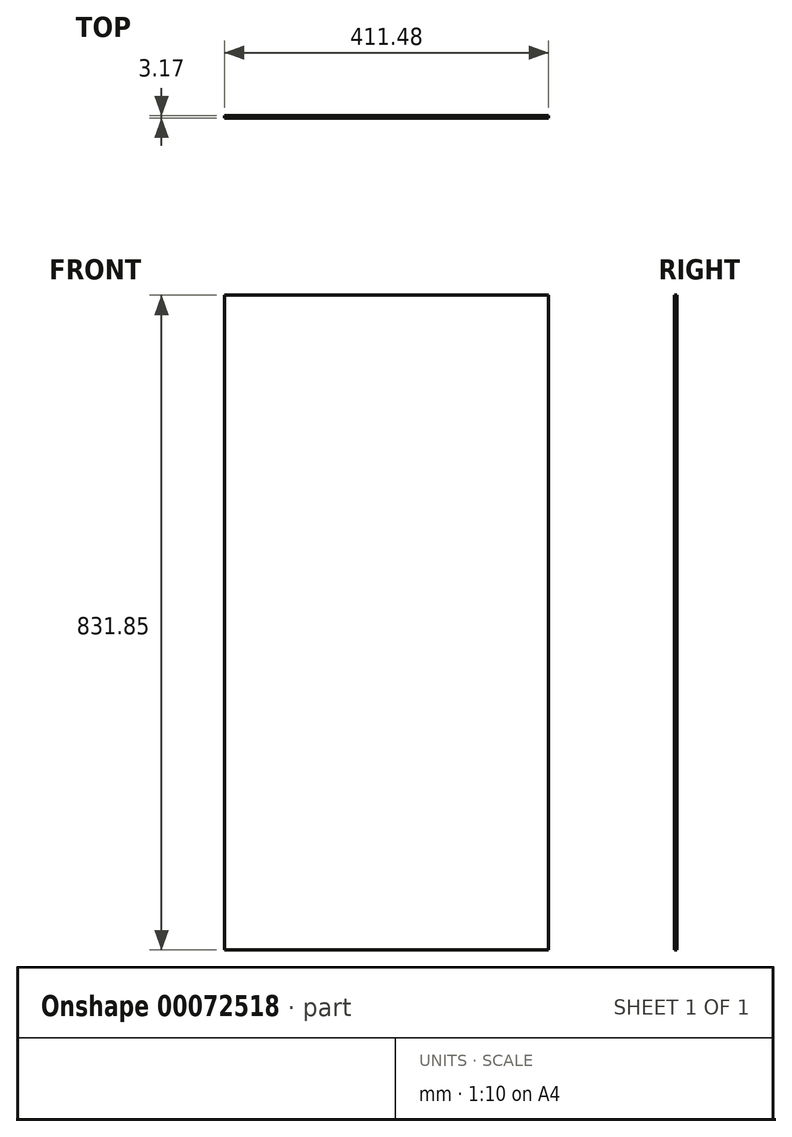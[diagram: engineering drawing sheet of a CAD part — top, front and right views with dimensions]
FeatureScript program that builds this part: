
annotation { "Feature Type Name" : "Feature", "Feature Type Description" : "" }
export const myFeature = defineFeature(function(context is Context, id is Id, definition is map)
    precondition{}
    {
        {
            var Q0;
            Q0=qCreatedBy(makeId("Front.planeOp"),FACE);
            var sketch = newSketch(context, id + "F0", { "sketchPlane" : qUnion([Q0])});
            skLineSegment(sketch, "E0.bottom", {"start": v(-329.27, 439.23) * mm, "end": v(82.2, 439.23) * mm});
            skLineSegment(sketch, "E0.top", {"start": v(-329.27, -392.62) * mm, "end": v(82.2, -392.62) * mm});
            skLineSegment(sketch, "E0.left", {"start": v(-329.27, 439.23) * mm, "end": v(-329.27, -392.62) * mm});
            skLineSegment(sketch, "E0.right", {"start": v(82.2, 439.23) * mm, "end": v(82.2, -392.62) * mm});
            skSolve(sketch);
        }
        {
            var Q0;
            Q0 = qSketchRegion(id + "F0", true);
            extrude(context, id + "F1", {"entities" : qUnion([Q0]), "depth" : 3.17 * mm});
        }
    });
